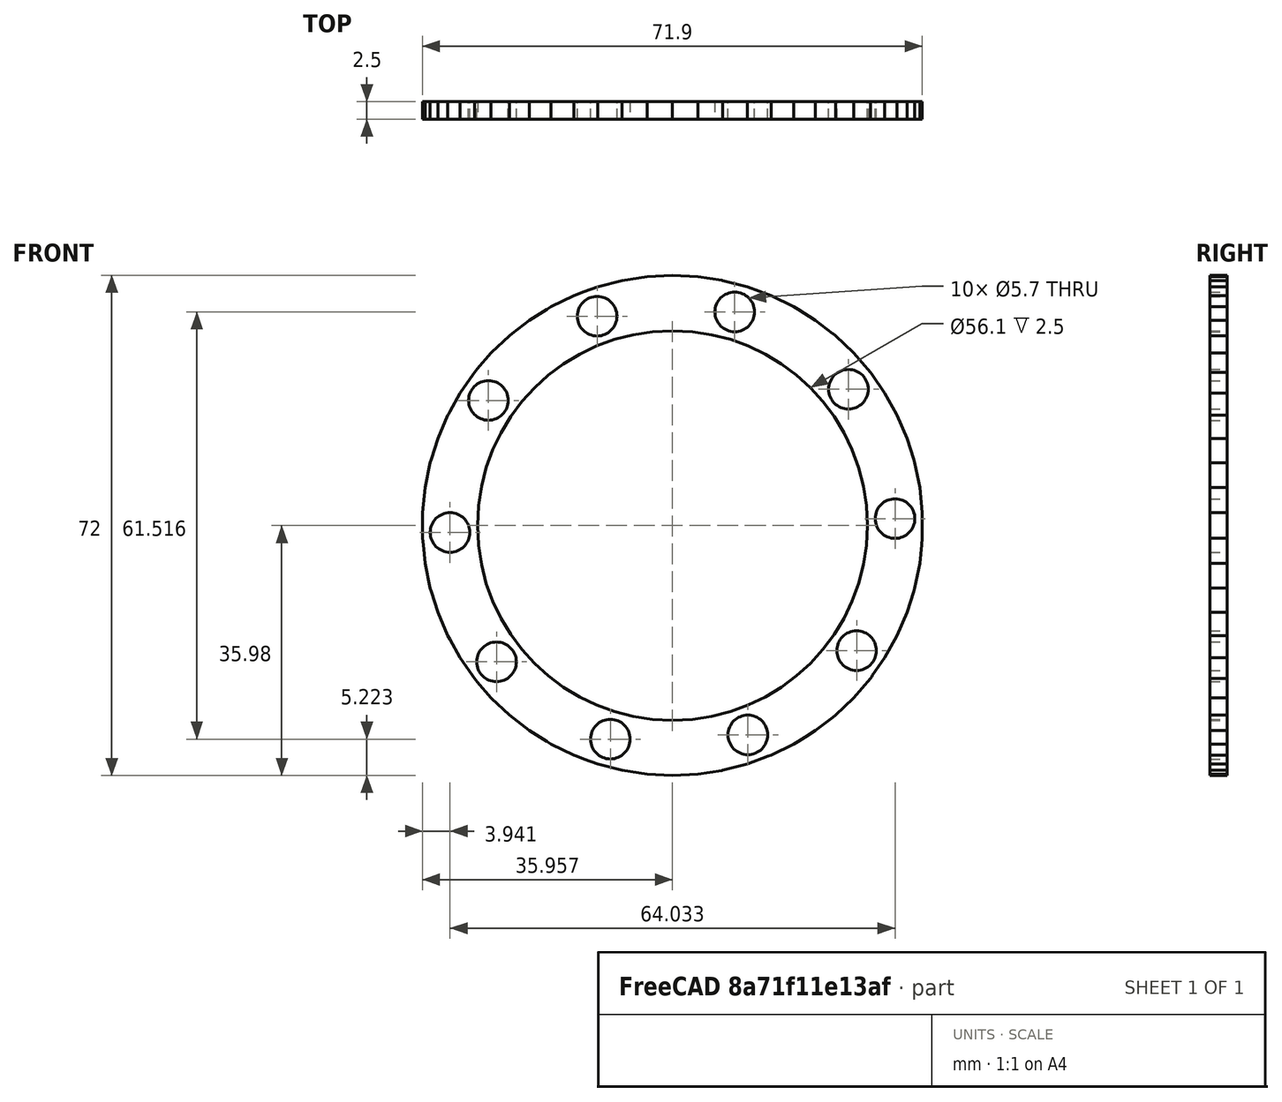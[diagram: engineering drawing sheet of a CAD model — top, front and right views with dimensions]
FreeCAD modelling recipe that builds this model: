
FCSTD DOCUMENT  (FreeCAD 0.21R33668 +26 (Git))
Label: Base_Bearing_Holder
License: All rights reserved
LicenseURL: https://en.wikipedia.org/wiki/All_rights_reserved
objects: Sketcher::SketchObject×2, PartDesign::Pocket×2, Part::Feature×1, PartDesign::FeatureBase×1, PartDesign::PolarPattern×1, PartDesign::Body×1
note: 10 computed .brp shape members not serialized (recipe doc carries the construction recipe); baked Part::Feature solids carry a one-line shape summary decoded from their .brp

FEATURE [Part::Feature] Part__Feature  label="Base_Bearing_Holder002 (Solid)"
  shape: bbox 71.91 x 2.5 x 72 mm, 574 faces (baked)
FEATURE [PartDesign::FeatureBase] BaseFeature
  BaseFeature = -> Part__Feature
FEATURE [Sketcher::SketchObject] Sketch
  ExternalGeometry = -> [BaseFeature]
  FullyConstrained = false
  MapMode = 5
  Placement = pos=(0,2.5,0) rot=(0,0.707107,0.707107;3.14159rad)
  Support = -> [BaseFeature]
  sketch-geometry (1):
    g0: Circle CenterX=-36.0072 CenterY=35.9803 CenterZ=0 NormalX=0 NormalY=0 NormalZ=1 AngleXU=0 Radius=28.05
  constraints (1):
    c: Diameter(g0) = 56.1
FEATURE [PartDesign::Pocket] Pocket
  BaseFeature = -> BaseFeature
  Direction = (0,-1,-2e-16)
  Length = 5
  Length2 = 5
  Profile = -> Sketch
  ReferenceAxis = -> Sketch [N_Axis]
  Type = 1
FEATURE [Sketcher::SketchObject] Sketch001
  ExternalGeometry = -> [Pocket]
  FullyConstrained = false
  MapMode = 5
  Placement = pos=(0,2.5,0) rot=(0,0.707107,0.707107;3.14159rad)
  Support = -> [Pocket]
  sketch-geometry (1):
    g0: Circle CenterX=-44.9524 CenterY=66.738 CenterZ=0 NormalX=0 NormalY=0 NormalZ=1 AngleXU=0 Radius=2.85
  constraints (1):
    c: Diameter(g0) = 5.7
FEATURE [PartDesign::Pocket] Pocket001
  BaseFeature = -> Pocket
  Direction = (0,-1,-2e-16)
  Length = 5
  Length2 = 5
  Profile = -> Sketch001
  ReferenceAxis = -> Sketch001 [N_Axis]
  Type = 1
FEATURE [PartDesign::PolarPattern] PolarPattern
  Angle = 360
  Axis = -> Pocket001 [Edge1209]
  BaseFeature = -> Pocket001
  Occurrences = 10
  Originals = -> [Pocket001]
FEATURE [PartDesign::Body] Body
  BaseFeature = -> Part__Feature
  Group = -> [BaseFeature,Sketch,Pocket,Sketch001,Pocket001,PolarPattern]
  Origin = -> Origin
  Tip = -> PolarPattern
